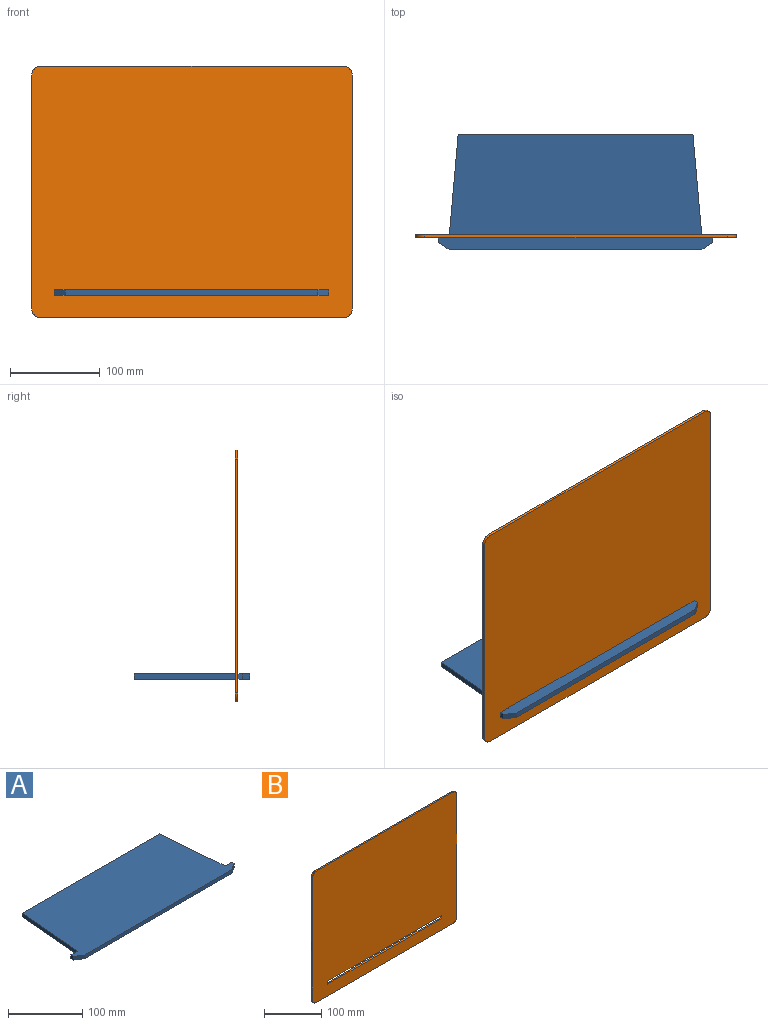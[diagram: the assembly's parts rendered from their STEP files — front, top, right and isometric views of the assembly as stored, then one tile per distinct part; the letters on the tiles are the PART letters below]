
ASSEMBLY  parts=2 mates=1
PART A: 12 faces, bbox 305x128x6 mm
  f0: plane 115x10.06mm, normal (1,0.09,0), area 692.6mm2, adj f1,f9,f10,f11
  f1: plane 12x6mm, normal (0,1,0), area 72mm2, adj f0,f2,f10,f11
  f2: plane 6x5mm, normal (1,0,0), area 30mm2, adj f1,f3,f10,f11
  f3: plane 12x8mm, normal (0.55,-0.83,0), area 86.5mm2, adj f2,f4,f10,f11
  f4: plane 281x6mm, normal (0,-1,0), area 1686mm2, adj f3,f5,f10,f11
  f5: plane 12x8mm, normal (-0.55,-0.83,0), area 86.5mm2, adj f4,f6,f10,f11
  f6: plane 6x5mm, normal (-1,0,0), area 30mm2, adj f5,f7,f10,f11
  f7: plane 12x6mm, normal (0,1,0), area 72mm2, adj f6,f8,f10,f11
  f8: plane 115x10.06mm, normal (-1,0.09,0), area 692.6mm2, adj f7,f9,f10,f11
  f9: plane 260.88x6mm, normal (0,1,0), area 1565.3mm2, adj f0,f8,f10,f11
  f10: plane 305x128mm, normal (0,0,-1), area 35027mm2, adj f0,f1,f2,f3,f4,f5,f6,f7
  f11: plane 305x128mm, normal (0,0,1), area 35027mm2, adj f0,f1,f2,f3,f4,f5,f6,f7
PART B: 18 faces, bbox 356x3x280 mm
  f0: plane 336x3mm, normal (0,0,-1), area 1008mm2, adj f8,f9,f12,f13
  f1: plane 260x3mm, normal (-1,0,0), area 780mm2, adj f8,f9,f13,f14
  f2: plane 336x3mm, normal (0,0,1), area 1008mm2, adj f8,f9,f14,f15
  f3: plane 5.5x3mm, normal (-1,0,0), area 16.5mm2, adj f8,f9,f10,f17
  f4: plane 279x3mm, normal (0,0,-1), area 837mm2, adj f8,f9,f10,f11
  f5: plane 5.5x3mm, normal (1,0,0), area 16.5mm2, adj f8,f9,f11,f16
  f6: plane 279x3mm, normal (0,0,1), area 837mm2, adj f8,f9,f16,f17
  f7: plane 260x3mm, normal (1,0,0), area 780mm2, adj f8,f9,f12,f15
  f8: plane 356x280mm, normal (0,1,0), area 97774.4mm2, adj f0,f1,f2,f3,f4,f5,f6,f7
  f9: plane 356x280mm, normal (0,-1,0), area 97774.4mm2, adj f0,f1,f2,f3,f4,f5,f6,f7
  f10: cylinder r=0.5mm len=3mm, axis (0,-1,0), area 2.4mm2, adj f3,f4,f8,f9
  f11: cylinder r=0.5mm len=3mm, axis (0,1,0), area 2.4mm2, adj f4,f5,f8,f9
  f12: cylinder r=10mm len=10mm, axis (0,-1,0), area 47.1mm2, adj f0,f7,f8,f9
  f13: cylinder r=10mm len=10mm, axis (0,1,0), area 47.1mm2, adj f0,f1,f8,f9
  f14: cylinder r=10mm len=10mm, axis (0,-1,0), area 47.1mm2, adj f1,f2,f8,f9
  f15: cylinder r=10mm len=10mm, axis (0,1,0), area 47.1mm2, adj f2,f7,f8,f9
  f16: cylinder r=0.5mm len=3mm, axis (0,-1,0), area 2.4mm2, adj f5,f6,f8,f9
  f17: cylinder r=0.5mm len=3mm, axis (0,1,0), area 2.4mm2, adj f3,f6,f8,f9
PLACE A t=(-24.11,-89.29,-0.62)mm
PLACE B t=(-23.61,-201.29,114.13)mm
MATE fastened B.f9 <-> A.f1  axis (0,-1,0) through (116.39,-204.29,2.38)mm
